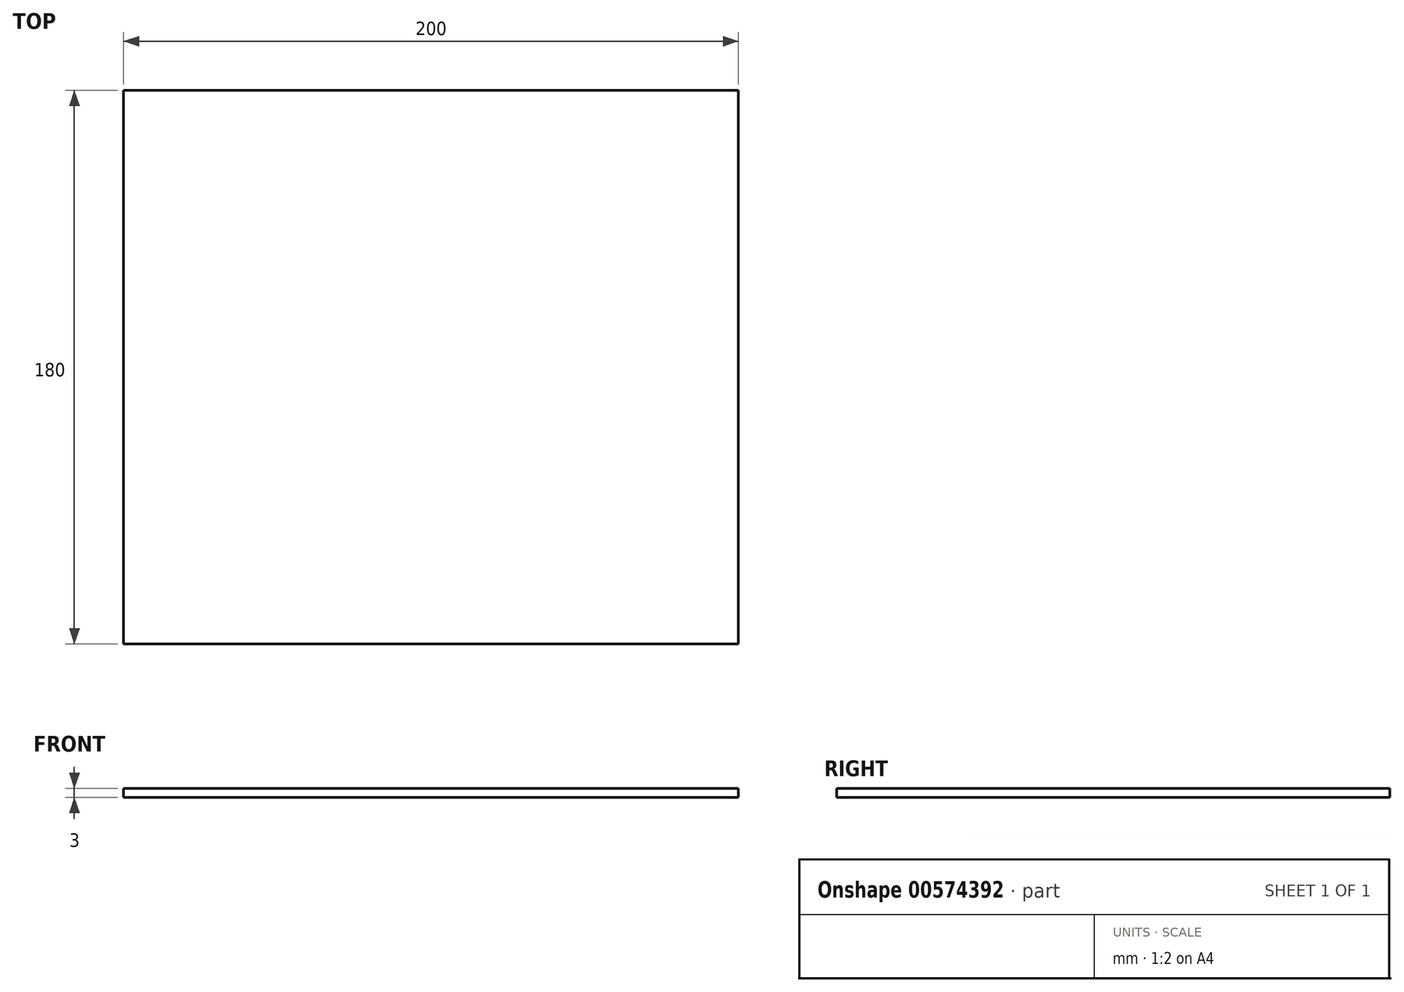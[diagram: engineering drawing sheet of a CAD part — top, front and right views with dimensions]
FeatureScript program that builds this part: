
annotation { "Feature Type Name" : "Feature", "Feature Type Description" : "" }
export const myFeature = defineFeature(function(context is Context, id is Id, definition is map)
    precondition{}
    {
        {
            var Q0;
            Q0=qCreatedBy(makeId("Top.planeOp"),FACE);
            var sketch = newSketch(context, id + "F0", { "sketchPlane" : qUnion([Q0])});
            skLineSegment(sketch, "E0.bottom", {"start": v(-161.04, 143.5) * mm, "end": v(38.96, 143.5) * mm});
            skLineSegment(sketch, "E0.top", {"start": v(-161.04, -36.5) * mm, "end": v(38.96, -36.5) * mm});
            skLineSegment(sketch, "E0.left", {"start": v(-161.04, 143.5) * mm, "end": v(-161.04, -36.5) * mm});
            skLineSegment(sketch, "E0.right", {"start": v(38.96, 143.5) * mm, "end": v(38.96, -36.5) * mm});
            skSolve(sketch);
        }
        {
            var Q0;
            Q0=makeQuery(id+"F0.imprint","IMPRINT",FACE,{"disambiguationData":[TD([[makeQuery(id+"F0.imprint","IMPRINT",EDGE,{"derivedFrom":sQuery(id+"F0.wireOp",EDGE,"E0.bottom")}),-1.0]])]});
            extrude(context, id + "F1", {"entities" : qUnion([Q0]), "depth" : 3 * mm, "offsetDistance" : 25 * mm});
        }
    });
